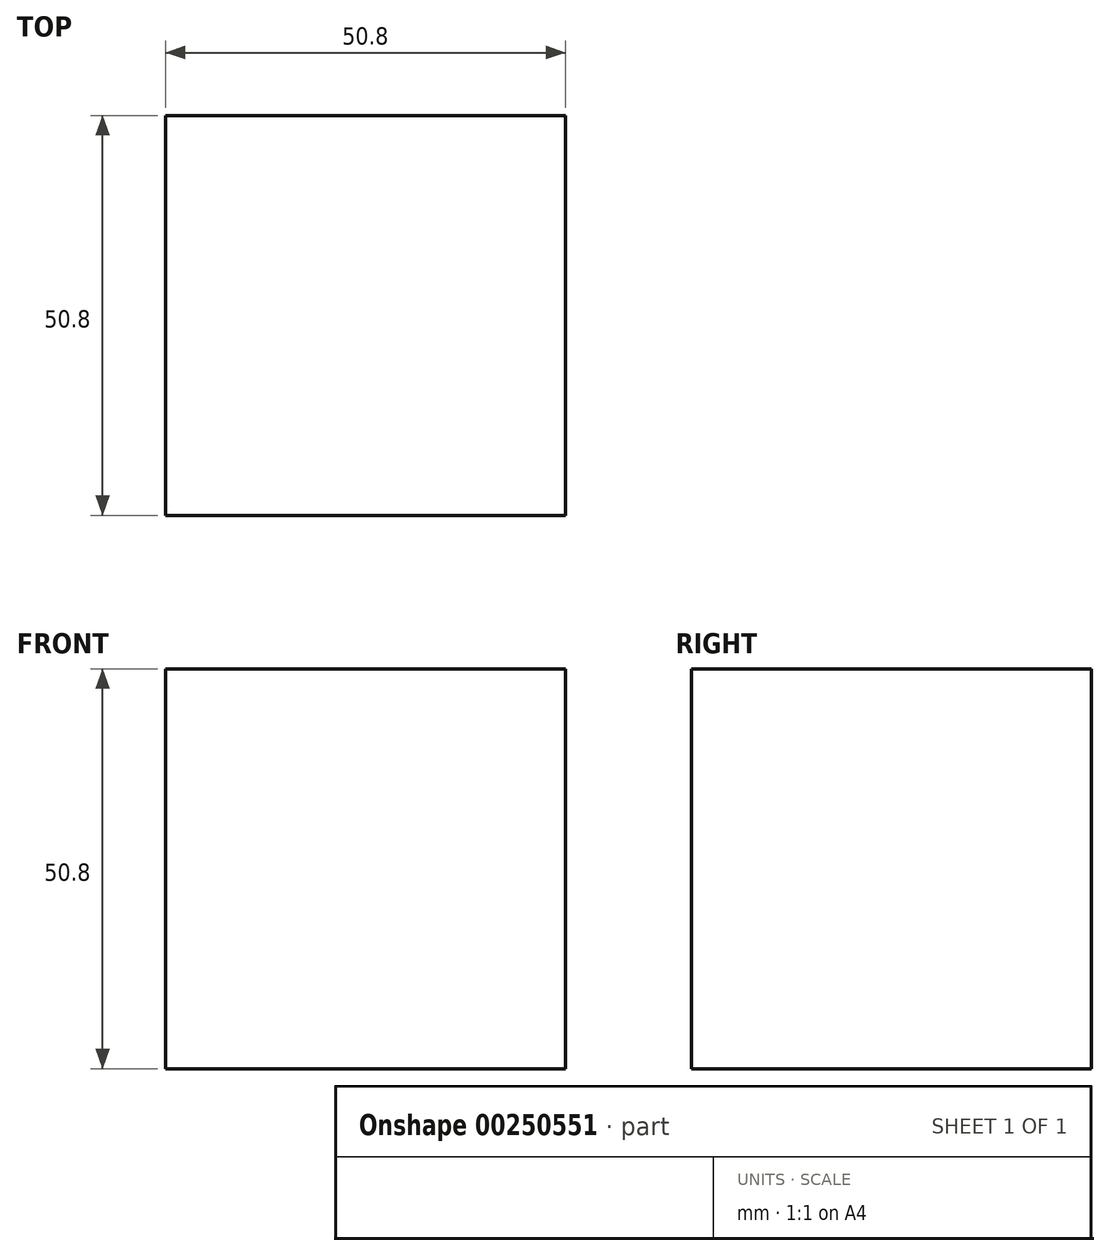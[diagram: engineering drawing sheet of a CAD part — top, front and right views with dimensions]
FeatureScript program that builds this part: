
annotation { "Feature Type Name" : "Feature", "Feature Type Description" : "" }
export const myFeature = defineFeature(function(context is Context, id is Id, definition is map)
    precondition{}
    {
        {
            var Q0;
            Q0=qCreatedBy(makeId("Front.planeOp"),FACE);
            var sketch = newSketch(context, id + "F0", { "sketchPlane" : qUnion([Q0])});
            skLineSegment(sketch, "E0.bottom", {"start": v(0, 0) * mm, "end": v(-50.8, 0) * mm});
            skLineSegment(sketch, "E0.top", {"start": v(0, 50.8) * mm, "end": v(-50.8, 50.8) * mm});
            skLineSegment(sketch, "E0.left", {"start": v(0, 0) * mm, "end": v(0, 50.8) * mm});
            skLineSegment(sketch, "E0.right", {"start": v(-50.8, 0) * mm, "end": v(-50.8, 50.8) * mm});
            skSolve(sketch);
        }
        {
            var Q0;
            Q0 = qSketchRegion(id + "F0", true);
            extrude(context, id + "F1", {"entities" : qUnion([Q0]), "endBound" : BoundingType.SYMMETRIC, "depth" : 50.8 * mm});
        }
    });
